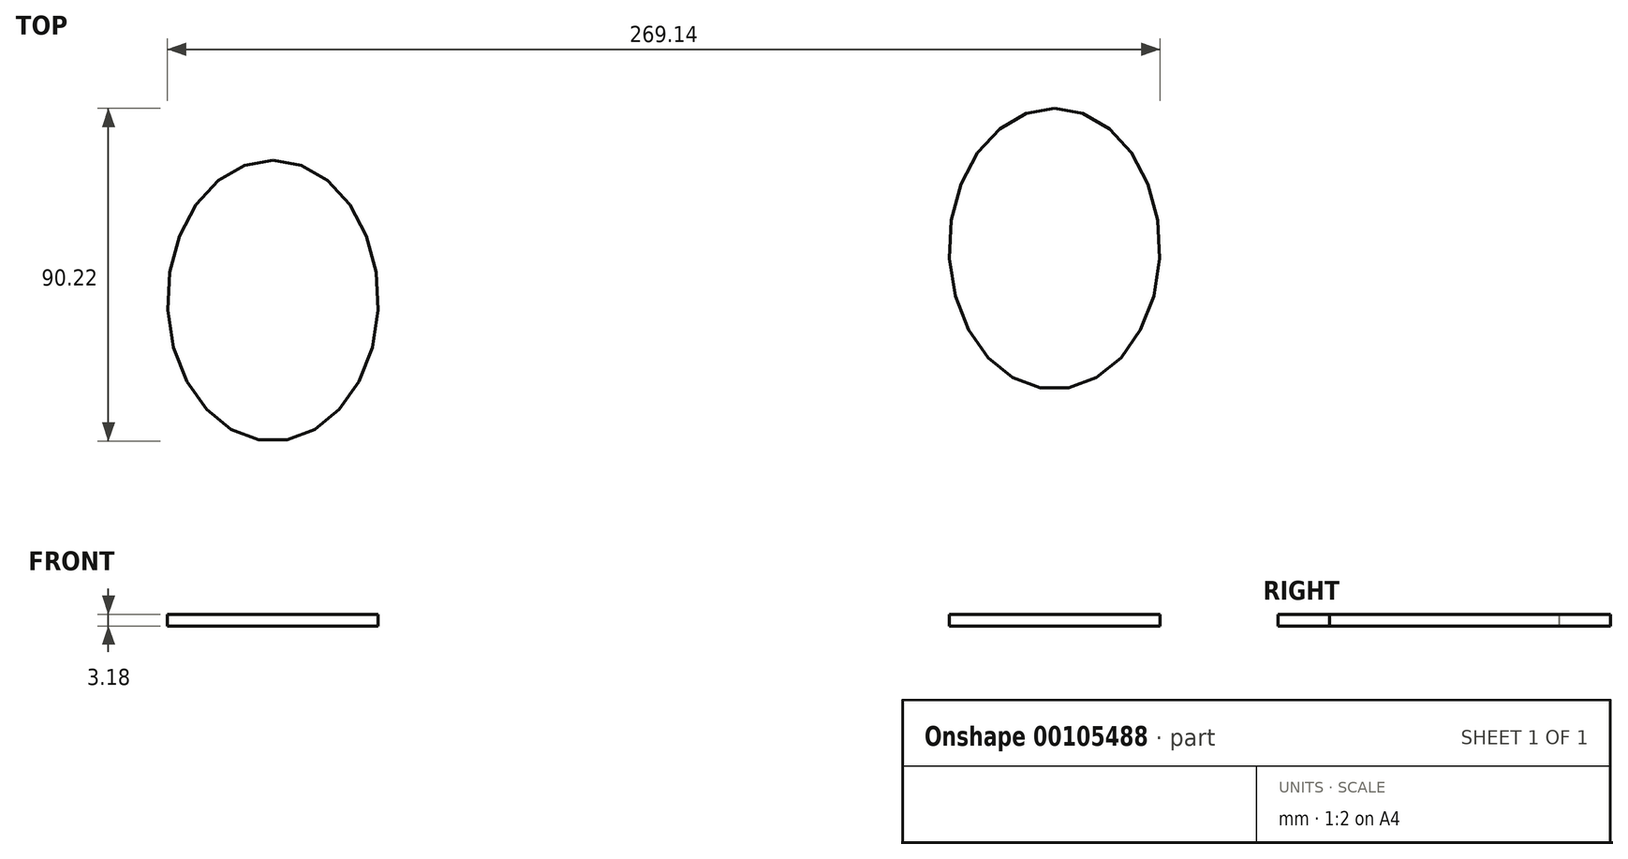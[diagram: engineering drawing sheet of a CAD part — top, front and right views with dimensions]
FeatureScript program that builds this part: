
annotation { "Feature Type Name" : "Feature", "Feature Type Description" : "" }
export const myFeature = defineFeature(function(context is Context, id is Id, definition is map)
    precondition{}
    {
        {
            var Q0;
            Q0=qCreatedBy(makeId("Top.planeOp"),FACE);
            var sketch = newSketch(context, id + "F0", { "sketchPlane" : qUnion([Q0])});
            skEllipse(sketch, "E0", {"center": v(0, 0) * mm, "majorRadius": 38.1 * mm, "minorRadius": 28.58 * mm, "majorAxis": v(0, 1)});
            skFitSpline(sketch, "E1.0", {"points": [v(1.84, 44.4) * mm, v(0, 44.47) * mm, v(-1.84, 44.4) * mm, v(-4.27, 44.17) * mm, v(-7.26, 43.57) * mm, v(-10.72, 42.4) * mm, v(-14.03, 40.82) * mm, v(-17.17, 38.85) * mm, v(-20.1, 36.5) * mm, v(-22.38, 34.26) * mm, v(-24.08, 32.3) * mm, v(-25.3, 30.76) * mm, v(-26.45, 29.15) * mm, v(-27.89, 26.92) * mm, v(-29.5, 24) * mm, v(-31.15, 20.33) * mm, v(-32.51, 16.49) * mm, v(-33.58, 12.51) * mm, v(-34.35, 8.42) * mm, v(-34.74, 4.94) * mm, v(-34.9, 2.13) * mm, v(-34.94, 0) * mm, v(-34.9, -2.13) * mm, v(-34.74, -4.94) * mm, v(-34.35, -8.42) * mm, v(-33.58, -12.51) * mm, v(-32.51, -16.49) * mm, v(-31.15, -20.33) * mm, v(-29.5, -24) * mm, v(-27.89, -26.92) * mm, v(-26.45, -29.15) * mm, v(-25.3, -30.76) * mm, v(-24.08, -32.3) * mm, v(-22.38, -34.26) * mm, v(-20.1, -36.5) * mm, v(-17.17, -38.85) * mm, v(-14.03, -40.82) * mm, v(-10.72, -42.4) * mm, v(-7.26, -43.57) * mm, v(-4.27, -44.17) * mm, v(-1.84, -44.4) * mm, v(0, -44.47) * mm, v(1.84, -44.4) * mm, v(4.27, -44.17) * mm, v(7.26, -43.57) * mm, v(10.72, -42.4) * mm, v(14.03, -40.82) * mm, v(17.17, -38.85) * mm, v(20.1, -36.5) * mm, v(22.38, -34.26) * mm, v(24.08, -32.3) * mm, v(25.3, -30.76) * mm, v(26.45, -29.15) * mm, v(27.89, -26.92) * mm, v(29.5, -24) * mm, v(31.15, -20.33) * mm, v(32.51, -16.49) * mm, v(33.58, -12.51) * mm, v(34.35, -8.42) * mm, v(34.74, -4.94) * mm, v(34.9, -2.13) * mm, v(34.94, 0) * mm, v(34.9, 2.13) * mm, v(34.74, 4.94) * mm, v(34.35, 8.42) * mm, v(33.58, 12.51) * mm, v(32.51, 16.49) * mm, v(31.15, 20.33) * mm, v(29.5, 24) * mm, v(27.89, 26.92) * mm, v(26.45, 29.15) * mm, v(25.3, 30.76) * mm, v(24.08, 32.3) * mm, v(22.38, 34.26) * mm, v(20.1, 36.5) * mm, v(17.17, 38.85) * mm, v(14.03, 40.82) * mm, v(10.72, 42.4) * mm, v(7.26, 43.57) * mm, v(4.27, 44.17) * mm, v(1.84, 44.4) * mm, v(0, 44.47) * mm, v(-1.84, 44.4) * mm, v(1.84, 44.4) * mm]});
            skFitSpline(sketch, "E2.0", {"points": [v(2.26, 50.75) * mm, v(0, 50.82) * mm, v(-2.26, 50.75) * mm, v(-5.24, 50.45) * mm, v(-8.9, 49.72) * mm, v(-13.12, 48.3) * mm, v(-17.12, 46.4) * mm, v(-20.86, 44.03) * mm, v(-24.34, 41.25) * mm, v(-27, 38.63) * mm, v(-28.97, 36.36) * mm, v(-30.38, 34.57) * mm, v(-31.7, 32.72) * mm, v(-33.35, 30.17) * mm, v(-35.19, 26.85) * mm, v(-37.06, 22.69) * mm, v(-38.58, 18.37) * mm, v(-39.78, 13.92) * mm, v(-40.64, 9.37) * mm, v(-41.07, 5.5) * mm, v(-41.25, 2.36) * mm, v(-41.29, 0) * mm, v(-41.25, -2.36) * mm, v(-41.07, -5.5) * mm, v(-40.64, -9.37) * mm, v(-39.78, -13.92) * mm, v(-38.58, -18.37) * mm, v(-37.06, -22.69) * mm, v(-35.19, -26.85) * mm, v(-33.35, -30.17) * mm, v(-31.7, -32.72) * mm, v(-30.38, -34.57) * mm, v(-28.97, -36.36) * mm, v(-27, -38.63) * mm, v(-24.34, -41.25) * mm, v(-20.86, -44.03) * mm, v(-17.12, -46.4) * mm, v(-13.12, -48.3) * mm, v(-8.9, -49.72) * mm, v(-5.24, -50.45) * mm, v(-2.26, -50.75) * mm, v(0, -50.82) * mm, v(2.26, -50.75) * mm, v(5.24, -50.45) * mm, v(8.9, -49.72) * mm, v(13.12, -48.3) * mm, v(17.12, -46.4) * mm, v(20.86, -44.03) * mm, v(24.34, -41.25) * mm, v(27, -38.63) * mm, v(28.97, -36.36) * mm, v(30.38, -34.57) * mm, v(31.7, -32.72) * mm, v(33.35, -30.17) * mm, v(35.19, -26.85) * mm, v(37.06, -22.69) * mm, v(38.58, -18.37) * mm, v(39.78, -13.92) * mm, v(40.64, -9.37) * mm, v(41.07, -5.5) * mm, v(41.25, -2.36) * mm, v(41.29, 0) * mm, v(41.25, 2.36) * mm, v(41.07, 5.5) * mm, v(40.64, 9.37) * mm, v(39.78, 13.92) * mm, v(38.58, 18.37) * mm, v(37.06, 22.69) * mm, v(35.19, 26.85) * mm, v(33.35, 30.17) * mm, v(31.7, 32.72) * mm, v(30.38, 34.57) * mm, v(28.97, 36.36) * mm, v(27, 38.63) * mm, v(24.34, 41.25) * mm, v(20.86, 44.03) * mm, v(17.12, 46.4) * mm, v(13.12, 48.3) * mm, v(8.9, 49.72) * mm, v(5.24, 50.45) * mm, v(2.26, 50.75) * mm, v(0, 50.82) * mm, v(-2.26, 50.75) * mm, v(2.26, 50.75) * mm]});
            skFitSpline(sketch, "E3.0", {"points": [v(2.68, 57.1) * mm, v(0, 57.18) * mm, v(-2.68, 57.1) * mm, v(-6.22, 56.74) * mm, v(-10.54, 55.87) * mm, v(-15.51, 54.2) * mm, v(-20.2, 51.96) * mm, v(-24.56, 49.2) * mm, v(-28.57, 46) * mm, v(-31.61, 43) * mm, v(-33.86, 40.4) * mm, v(-35.46, 38.38) * mm, v(-36.96, 36.28) * mm, v(-38.82, 33.41) * mm, v(-40.88, 29.69) * mm, v(-42.96, 25.05) * mm, v(-44.65, 20.25) * mm, v(-45.98, 15.33) * mm, v(-46.92, 10.3) * mm, v(-47.4, 6.04) * mm, v(-47.6, 2.6) * mm, v(-47.64, 0) * mm, v(-47.6, -2.6) * mm, v(-47.4, -6.04) * mm, v(-46.92, -10.3) * mm, v(-45.98, -15.33) * mm, v(-44.65, -20.25) * mm, v(-42.96, -25.05) * mm, v(-40.88, -29.69) * mm, v(-38.82, -33.41) * mm, v(-36.96, -36.28) * mm, v(-35.46, -38.38) * mm, v(-33.86, -40.4) * mm, v(-31.61, -43) * mm, v(-28.57, -46) * mm, v(-24.56, -49.2) * mm, v(-20.2, -51.96) * mm, v(-15.51, -54.2) * mm, v(-10.54, -55.87) * mm, v(-6.22, -56.74) * mm, v(-2.68, -57.1) * mm, v(0, -57.18) * mm, v(2.68, -57.1) * mm, v(6.22, -56.74) * mm, v(10.54, -55.87) * mm, v(15.51, -54.2) * mm, v(20.2, -51.96) * mm, v(24.56, -49.2) * mm, v(28.57, -46) * mm, v(31.61, -43) * mm, v(33.86, -40.4) * mm, v(35.46, -38.38) * mm, v(36.96, -36.28) * mm, v(38.82, -33.41) * mm, v(40.88, -29.69) * mm, v(42.96, -25.05) * mm, v(44.65, -20.25) * mm, v(45.98, -15.33) * mm, v(46.92, -10.3) * mm, v(47.4, -6.04) * mm, v(47.6, -2.6) * mm, v(47.64, 0) * mm, v(47.6, 2.6) * mm, v(47.4, 6.04) * mm, v(46.92, 10.3) * mm, v(45.98, 15.33) * mm, v(44.65, 20.25) * mm, v(42.96, 25.05) * mm, v(40.88, 29.69) * mm, v(38.82, 33.41) * mm, v(36.96, 36.28) * mm, v(35.46, 38.38) * mm, v(33.86, 40.4) * mm, v(31.61, 43) * mm, v(28.57, 46) * mm, v(24.56, 49.2) * mm, v(20.2, 51.96) * mm, v(15.51, 54.2) * mm, v(10.54, 55.87) * mm, v(6.22, 56.74) * mm, v(2.68, 57.1) * mm, v(0, 57.18) * mm, v(-2.68, 57.1) * mm, v(2.68, 57.1) * mm]});
            skFitSpline(sketch, "E4.0", {"points": [v(3.1, 63.43) * mm, v(0, 63.53) * mm, v(-3.1, 63.43) * mm, v(-7.19, 63.02) * mm, v(-12.19, 62.03) * mm, v(-17.91, 60.1) * mm, v(-23.28, 57.53) * mm, v(-28.25, 54.39) * mm, v(-32.8, 50.75) * mm, v(-36.23, 47.36) * mm, v(-38.76, 44.46) * mm, v(-40.54, 42.2) * mm, v(-42.22, 39.85) * mm, v(-44.28, 36.65) * mm, v(-46.57, 32.53) * mm, v(-48.86, 27.4) * mm, v(-50.73, 22.14) * mm, v(-52.17, 16.74) * mm, v(-53.2, 11.25) * mm, v(-53.73, 6.6) * mm, v(-53.94, 2.84) * mm, v(-54, 0) * mm, v(-53.94, -2.84) * mm, v(-53.73, -6.6) * mm, v(-53.2, -11.25) * mm, v(-52.17, -16.74) * mm, v(-50.73, -22.14) * mm, v(-48.86, -27.4) * mm, v(-46.57, -32.53) * mm, v(-44.28, -36.65) * mm, v(-42.22, -39.85) * mm, v(-40.54, -42.2) * mm, v(-38.76, -44.46) * mm, v(-36.23, -47.36) * mm, v(-32.8, -50.75) * mm, v(-28.25, -54.39) * mm, v(-23.28, -57.53) * mm, v(-17.91, -60.1) * mm, v(-12.19, -62.03) * mm, v(-7.19, -63.02) * mm, v(-3.1, -63.43) * mm, v(0, -63.53) * mm, v(3.1, -63.43) * mm, v(7.19, -63.02) * mm, v(12.19, -62.03) * mm, v(17.91, -60.1) * mm, v(23.28, -57.53) * mm, v(28.25, -54.39) * mm, v(32.8, -50.75) * mm, v(36.23, -47.36) * mm, v(38.76, -44.46) * mm, v(40.54, -42.2) * mm, v(42.22, -39.85) * mm, v(44.28, -36.65) * mm, v(46.57, -32.53) * mm, v(48.86, -27.4) * mm, v(50.73, -22.14) * mm, v(52.17, -16.74) * mm, v(53.2, -11.25) * mm, v(53.73, -6.6) * mm, v(53.94, -2.84) * mm, v(54, 0) * mm, v(53.94, 2.84) * mm, v(53.73, 6.6) * mm, v(53.2, 11.25) * mm, v(52.17, 16.74) * mm, v(50.73, 22.14) * mm, v(48.86, 27.4) * mm, v(46.57, 32.53) * mm, v(44.28, 36.65) * mm, v(42.22, 39.85) * mm, v(40.54, 42.2) * mm, v(38.76, 44.46) * mm, v(36.23, 47.36) * mm, v(32.8, 50.75) * mm, v(28.25, 54.39) * mm, v(23.28, 57.53) * mm, v(17.91, 60.1) * mm, v(12.19, 62.03) * mm, v(7.19, 63.02) * mm, v(3.1, 63.43) * mm, v(0, 63.53) * mm, v(-3.1, 63.43) * mm, v(3.1, 63.43) * mm]});
            skFitSpline(sketch, "E5.0", {"points": [v(3.52, 69.77) * mm, v(0, 69.89) * mm, v(-3.52, 69.77) * mm, v(-8.16, 69.31) * mm, v(-13.83, 68.18) * mm, v(-20.3, 66) * mm, v(-26.36, 63.1) * mm, v(-31.95, 59.57) * mm, v(-37.03, 55.5) * mm, v(-40.85, 51.73) * mm, v(-43.65, 48.51) * mm, v(-45.63, 46) * mm, v(-47.47, 43.42) * mm, v(-49.75, 39.9) * mm, v(-52.25, 35.37) * mm, v(-54.76, 29.76) * mm, v(-56.8, 24.02) * mm, v(-58.37, 18.16) * mm, v(-59.5, 12.19) * mm, v(-60.06, 7.14) * mm, v(-60.29, 3.07) * mm, v(-60.34, 0) * mm, v(-60.29, -3.07) * mm, v(-60.06, -7.14) * mm, v(-59.5, -12.19) * mm, v(-58.37, -18.16) * mm, v(-56.8, -24.02) * mm, v(-54.76, -29.76) * mm, v(-52.25, -35.37) * mm, v(-49.75, -39.9) * mm, v(-47.47, -43.42) * mm, v(-45.63, -46) * mm, v(-43.65, -48.51) * mm, v(-40.85, -51.73) * mm, v(-37.03, -55.5) * mm, v(-31.95, -59.57) * mm, v(-26.36, -63.1) * mm, v(-20.3, -66) * mm, v(-13.83, -68.18) * mm, v(-8.16, -69.31) * mm, v(-3.52, -69.77) * mm, v(0, -69.89) * mm, v(3.52, -69.77) * mm, v(8.16, -69.31) * mm, v(13.83, -68.18) * mm, v(20.3, -66) * mm, v(26.36, -63.1) * mm, v(31.95, -59.57) * mm, v(37.03, -55.5) * mm, v(40.85, -51.73) * mm, v(43.65, -48.51) * mm, v(45.63, -46) * mm, v(47.47, -43.42) * mm, v(49.75, -39.9) * mm, v(52.25, -35.37) * mm, v(54.76, -29.76) * mm, v(56.8, -24.02) * mm, v(58.37, -18.16) * mm, v(59.5, -12.19) * mm, v(60.06, -7.14) * mm, v(60.29, -3.07) * mm, v(60.34, 0) * mm, v(60.29, 3.07) * mm, v(60.06, 7.14) * mm, v(59.5, 12.19) * mm, v(58.37, 18.16) * mm, v(56.8, 24.02) * mm, v(54.76, 29.76) * mm, v(52.25, 35.37) * mm, v(49.75, 39.9) * mm, v(47.47, 43.42) * mm, v(45.63, 46) * mm, v(43.65, 48.51) * mm, v(40.85, 51.73) * mm, v(37.03, 55.5) * mm, v(31.95, 59.57) * mm, v(26.36, 63.1) * mm, v(20.3, 66) * mm, v(13.83, 68.18) * mm, v(8.16, 69.31) * mm, v(3.52, 69.77) * mm, v(0, 69.89) * mm, v(-3.52, 69.77) * mm, v(3.52, 69.77) * mm]});
            skFitSpline(sketch, "E6.0", {"points": [v(3.94, 76.11) * mm, v(0, 76.24) * mm, v(-3.94, 76.11) * mm, v(-9.14, 75.6) * mm, v(-15.48, 74.33) * mm, v(-22.7, 71.9) * mm, v(-29.45, 68.67) * mm, v(-35.64, 64.75) * mm, v(-41.27, 60.25) * mm, v(-45.47, 56.1) * mm, v(-48.54, 52.56) * mm, v(-50.71, 49.81) * mm, v(-52.73, 46.99) * mm, v(-55.21, 43.14) * mm, v(-57.94, 38.2) * mm, v(-60.67, 32.12) * mm, v(-62.87, 25.9) * mm, v(-64.57, 19.57) * mm, v(-65.78, 13.13) * mm, v(-66.39, 7.7) * mm, v(-66.63, 3.3) * mm, v(-66.7, 0) * mm, v(-66.63, -3.3) * mm, v(-66.39, -7.7) * mm, v(-65.78, -13.13) * mm, v(-64.57, -19.57) * mm, v(-62.87, -25.9) * mm, v(-60.67, -32.12) * mm, v(-57.94, -38.2) * mm, v(-55.21, -43.14) * mm, v(-52.73, -46.99) * mm, v(-50.71, -49.81) * mm, v(-48.54, -52.56) * mm, v(-45.47, -56.1) * mm, v(-41.27, -60.25) * mm, v(-35.64, -64.75) * mm, v(-29.45, -68.67) * mm, v(-22.7, -71.9) * mm, v(-15.48, -74.33) * mm, v(-9.14, -75.6) * mm, v(-3.94, -76.11) * mm, v(0, -76.24) * mm, v(3.94, -76.11) * mm, v(9.14, -75.6) * mm, v(15.48, -74.33) * mm, v(22.7, -71.9) * mm, v(29.45, -68.67) * mm, v(35.64, -64.75) * mm, v(41.27, -60.25) * mm, v(45.47, -56.1) * mm, v(48.54, -52.56) * mm, v(50.71, -49.81) * mm, v(52.73, -46.99) * mm, v(55.21, -43.14) * mm, v(57.94, -38.2) * mm, v(60.67, -32.12) * mm, v(62.87, -25.9) * mm, v(64.57, -19.57) * mm, v(65.78, -13.13) * mm, v(66.39, -7.7) * mm, v(66.63, -3.3) * mm, v(66.7, 0) * mm, v(66.63, 3.3) * mm, v(66.39, 7.7) * mm, v(65.78, 13.13) * mm, v(64.57, 19.57) * mm, v(62.87, 25.9) * mm, v(60.67, 32.12) * mm, v(57.94, 38.2) * mm, v(55.21, 43.14) * mm, v(52.73, 46.99) * mm, v(50.71, 49.81) * mm, v(48.54, 52.56) * mm, v(45.47, 56.1) * mm, v(41.27, 60.25) * mm, v(35.64, 64.75) * mm, v(29.45, 68.67) * mm, v(22.7, 71.9) * mm, v(15.48, 74.33) * mm, v(9.14, 75.6) * mm, v(3.94, 76.11) * mm, v(0, 76.24) * mm, v(-3.94, 76.11) * mm, v(3.94, 76.11) * mm]});
            skFitSpline(sketch, "E7.0", {"points": [v(4.36, 82.45) * mm, v(0, 82.6) * mm, v(-4.36, 82.45) * mm, v(-10.1, 81.88) * mm, v(-17.12, 80.48) * mm, v(-25.1, 77.8) * mm, v(-32.53, 74.23) * mm, v(-39.34, 69.93) * mm, v(-45.5, 65) * mm, v(-50.09, 60.47) * mm, v(-53.44, 56.61) * mm, v(-55.8, 53.62) * mm, v(-57.98, 50.55) * mm, v(-60.67, 46.38) * mm, v(-63.63, 41.05) * mm, v(-66.57, 34.48) * mm, v(-68.94, 27.79) * mm, v(-70.77, 20.98) * mm, v(-72.07, 14.07) * mm, v(-72.72, 8.25) * mm, v(-72.98, 3.54) * mm, v(-73.05, 0) * mm, v(-72.98, -3.54) * mm, v(-72.72, -8.25) * mm, v(-72.07, -14.07) * mm, v(-70.77, -20.98) * mm, v(-68.94, -27.79) * mm, v(-66.57, -34.48) * mm, v(-63.63, -41.05) * mm, v(-60.67, -46.38) * mm, v(-57.98, -50.55) * mm, v(-55.8, -53.62) * mm, v(-53.44, -56.61) * mm, v(-50.09, -60.47) * mm, v(-45.5, -65) * mm, v(-39.34, -69.93) * mm, v(-32.53, -74.23) * mm, v(-25.1, -77.8) * mm, v(-17.12, -80.48) * mm, v(-10.1, -81.88) * mm, v(-4.36, -82.45) * mm, v(0, -82.6) * mm, v(4.36, -82.45) * mm, v(10.1, -81.88) * mm, v(17.12, -80.48) * mm, v(25.1, -77.8) * mm, v(32.53, -74.23) * mm, v(39.34, -69.93) * mm, v(45.5, -65) * mm, v(50.09, -60.47) * mm, v(53.44, -56.61) * mm, v(55.8, -53.62) * mm, v(57.98, -50.55) * mm, v(60.67, -46.38) * mm, v(63.63, -41.05) * mm, v(66.57, -34.48) * mm, v(68.94, -27.79) * mm, v(70.77, -20.98) * mm, v(72.07, -14.07) * mm, v(72.72, -8.25) * mm, v(72.98, -3.54) * mm, v(73.05, 0) * mm, v(72.98, 3.54) * mm, v(72.72, 8.25) * mm, v(72.07, 14.07) * mm, v(70.77, 20.98) * mm, v(68.94, 27.79) * mm, v(66.57, 34.48) * mm, v(63.63, 41.05) * mm, v(60.67, 46.38) * mm, v(57.98, 50.55) * mm, v(55.8, 53.62) * mm, v(53.44, 56.61) * mm, v(50.09, 60.47) * mm, v(45.5, 65) * mm, v(39.34, 69.93) * mm, v(32.53, 74.23) * mm, v(25.1, 77.8) * mm, v(17.12, 80.48) * mm, v(10.1, 81.88) * mm, v(4.36, 82.45) * mm, v(0, 82.6) * mm, v(-4.36, 82.45) * mm, v(4.36, 82.45) * mm]});
            skFitSpline(sketch, "E8.0", {"points": [v(4.78, 88.8) * mm, v(0, 88.95) * mm, v(-4.78, 88.8) * mm, v(-11.08, 88.17) * mm, v(-18.76, 86.63) * mm, v(-27.5, 83.7) * mm, v(-35.6, 79.8) * mm, v(-43.03, 75.11) * mm, v(-49.73, 69.76) * mm, v(-54.7, 64.83) * mm, v(-58.33, 60.67) * mm, v(-60.88, 57.43) * mm, v(-63.24, 54.12) * mm, v(-66.14, 49.63) * mm, v(-69.32, 43.89) * mm, v(-72.47, 36.84) * mm, v(-75.01, 29.67) * mm, v(-76.96, 22.39) * mm, v(-78.35, 15.01) * mm, v(-79.05, 8.8) * mm, v(-79.33, 3.78) * mm, v(-79.4, 0) * mm, v(-79.33, -3.78) * mm, v(-79.05, -8.8) * mm, v(-78.35, -15.01) * mm, v(-76.96, -22.39) * mm, v(-75.01, -29.67) * mm, v(-72.47, -36.84) * mm, v(-69.32, -43.89) * mm, v(-66.14, -49.63) * mm, v(-63.24, -54.12) * mm, v(-60.88, -57.43) * mm, v(-58.33, -60.67) * mm, v(-54.7, -64.83) * mm, v(-49.73, -69.76) * mm, v(-43.03, -75.11) * mm, v(-35.6, -79.8) * mm, v(-27.5, -83.7) * mm, v(-18.76, -86.63) * mm, v(-11.08, -88.17) * mm, v(-4.78, -88.8) * mm, v(0, -88.95) * mm, v(4.78, -88.8) * mm, v(11.08, -88.17) * mm, v(18.76, -86.63) * mm, v(27.5, -83.7) * mm, v(35.6, -79.8) * mm, v(43.03, -75.11) * mm, v(49.73, -69.76) * mm, v(54.7, -64.83) * mm, v(58.33, -60.67) * mm, v(60.88, -57.43) * mm, v(63.24, -54.12) * mm, v(66.14, -49.63) * mm, v(69.32, -43.89) * mm, v(72.47, -36.84) * mm, v(75.01, -29.67) * mm, v(76.96, -22.39) * mm, v(78.35, -15.01) * mm, v(79.05, -8.8) * mm, v(79.33, -3.78) * mm, v(79.4, 0) * mm, v(79.33, 3.78) * mm, v(79.05, 8.8) * mm, v(78.35, 15.01) * mm, v(76.96, 22.39) * mm, v(75.01, 29.67) * mm, v(72.47, 36.84) * mm, v(69.32, 43.89) * mm, v(66.14, 49.63) * mm, v(63.24, 54.12) * mm, v(60.88, 57.43) * mm, v(58.33, 60.67) * mm, v(54.7, 64.83) * mm, v(49.73, 69.76) * mm, v(43.03, 75.11) * mm, v(35.6, 79.8) * mm, v(27.5, 83.7) * mm, v(18.76, 86.63) * mm, v(11.08, 88.17) * mm, v(4.78, 88.8) * mm, v(0, 88.95) * mm, v(-4.78, 88.8) * mm, v(4.78, 88.8) * mm]});
            skFitSpline(sketch, "E9.0", {"points": [v(5.2, 95.14) * mm, v(0, 95.3) * mm, v(-5.2, 95.14) * mm, v(-12.06, 94.45) * mm, v(-20.4, 92.78) * mm, v(-29.9, 89.59) * mm, v(-38.7, 85.37) * mm, v(-46.72, 80.3) * mm, v(-53.96, 74.5) * mm, v(-59.32, 69.2) * mm, v(-63.22, 64.72) * mm, v(-65.96, 61.24) * mm, v(-68.5, 57.69) * mm, v(-71.6, 52.87) * mm, v(-75, 46.73) * mm, v(-78.38, 39.2) * mm, v(-81.08, 31.55) * mm, v(-83.16, 23.8) * mm, v(-84.64, 15.96) * mm, v(-85.38, 9.35) * mm, v(-85.68, 4.02) * mm, v(-85.75, 0) * mm, v(-85.68, -4.02) * mm, v(-85.38, -9.35) * mm, v(-84.64, -15.96) * mm, v(-83.16, -23.8) * mm, v(-81.08, -31.55) * mm, v(-78.38, -39.2) * mm, v(-75, -46.73) * mm, v(-71.6, -52.87) * mm, v(-68.5, -57.69) * mm, v(-65.96, -61.24) * mm, v(-63.22, -64.72) * mm, v(-59.32, -69.2) * mm, v(-53.96, -74.5) * mm, v(-46.72, -80.3) * mm, v(-38.7, -85.37) * mm, v(-29.9, -89.59) * mm, v(-20.4, -92.78) * mm, v(-12.06, -94.45) * mm, v(-5.2, -95.14) * mm, v(0, -95.3) * mm, v(5.2, -95.14) * mm, v(12.06, -94.45) * mm, v(20.4, -92.78) * mm, v(29.9, -89.59) * mm, v(38.7, -85.37) * mm, v(46.72, -80.3) * mm, v(53.96, -74.5) * mm, v(59.32, -69.2) * mm, v(63.22, -64.72) * mm, v(65.96, -61.24) * mm, v(68.5, -57.69) * mm, v(71.6, -52.87) * mm, v(75, -46.73) * mm, v(78.38, -39.2) * mm, v(81.08, -31.55) * mm, v(83.16, -23.8) * mm, v(84.64, -15.96) * mm, v(85.38, -9.35) * mm, v(85.68, -4.02) * mm, v(85.75, 0) * mm, v(85.68, 4.02) * mm, v(85.38, 9.35) * mm, v(84.64, 15.96) * mm, v(83.16, 23.8) * mm, v(81.08, 31.55) * mm, v(78.38, 39.2) * mm, v(75, 46.73) * mm, v(71.6, 52.87) * mm, v(68.5, 57.69) * mm, v(65.96, 61.24) * mm, v(63.22, 64.72) * mm, v(59.32, 69.2) * mm, v(53.96, 74.5) * mm, v(46.72, 80.3) * mm, v(38.7, 85.37) * mm, v(29.9, 89.59) * mm, v(20.4, 92.78) * mm, v(12.06, 94.45) * mm, v(5.2, 95.14) * mm, v(0, 95.3) * mm, v(-5.2, 95.14) * mm, v(5.2, 95.14) * mm]});
            skFitSpline(sketch, "E10.0", {"points": [v(5.62, 101.48) * mm, v(0, 101.66) * mm, v(-5.62, 101.48) * mm, v(-13.03, 100.74) * mm, v(-22.05, 98.93) * mm, v(-32.29, 95.49) * mm, v(-41.77, 90.94) * mm, v(-50.42, 85.47) * mm, v(-58.2, 79.26) * mm, v(-63.94, 73.57) * mm, v(-68.12, 68.77) * mm, v(-71.04, 65.06) * mm, v(-73.75, 61.26) * mm, v(-77.07, 56.12) * mm, v(-80.7, 49.57) * mm, v(-84.28, 41.56) * mm, v(-87.15, 33.44) * mm, v(-89.36, 25.21) * mm, v(-90.92, 16.9) * mm, v(-91.7, 9.9) * mm, v(-92.02, 4.25) * mm, v(-92.1, 0) * mm, v(-92.02, -4.25) * mm, v(-91.7, -9.9) * mm, v(-90.92, -16.9) * mm, v(-89.36, -25.21) * mm, v(-87.15, -33.44) * mm, v(-84.28, -41.56) * mm, v(-80.7, -49.57) * mm, v(-77.07, -56.12) * mm, v(-73.75, -61.26) * mm, v(-71.04, -65.06) * mm, v(-68.12, -68.77) * mm, v(-63.94, -73.57) * mm, v(-58.2, -79.26) * mm, v(-50.42, -85.47) * mm, v(-41.77, -90.94) * mm, v(-32.29, -95.49) * mm, v(-22.05, -98.93) * mm, v(-13.03, -100.74) * mm, v(-5.62, -101.48) * mm, v(0, -101.66) * mm, v(5.62, -101.48) * mm, v(13.03, -100.74) * mm, v(22.05, -98.93) * mm, v(32.29, -95.49) * mm, v(41.77, -90.94) * mm, v(50.42, -85.47) * mm, v(58.2, -79.26) * mm, v(63.94, -73.57) * mm, v(68.12, -68.77) * mm, v(71.04, -65.06) * mm, v(73.75, -61.26) * mm, v(77.07, -56.12) * mm, v(80.7, -49.57) * mm, v(84.28, -41.56) * mm, v(87.15, -33.44) * mm, v(89.36, -25.21) * mm, v(90.92, -16.9) * mm, v(91.7, -9.9) * mm, v(92.02, -4.25) * mm, v(92.1, 0) * mm, v(92.02, 4.25) * mm, v(91.7, 9.9) * mm, v(90.92, 16.9) * mm, v(89.36, 25.21) * mm, v(87.15, 33.44) * mm, v(84.28, 41.56) * mm, v(80.7, 49.57) * mm, v(77.07, 56.12) * mm, v(73.75, 61.26) * mm, v(71.04, 65.06) * mm, v(68.12, 68.77) * mm, v(63.94, 73.57) * mm, v(58.2, 79.26) * mm, v(50.42, 85.47) * mm, v(41.77, 90.94) * mm, v(32.29, 95.49) * mm, v(22.05, 98.93) * mm, v(13.03, 100.74) * mm, v(5.62, 101.48) * mm, v(0, 101.66) * mm, v(-5.62, 101.48) * mm, v(5.62, 101.48) * mm]});
            skEllipse(sketch, "E11", {"center": v(211.98, 14.02) * mm, "majorRadius": 38.1 * mm, "minorRadius": 28.58 * mm, "majorAxis": v(0, 1)});
            skFitSpline(sketch, "E12.0", {"points": [v(213.61, 55.25) * mm, v(211.98, 55.3) * mm, v(210.36, 55.25) * mm, v(208.2, 55.04) * mm, v(205.55, 54.51) * mm, v(202.46, 53.47) * mm, v(199.5, 52.05) * mm, v(196.66, 50.27) * mm, v(194, 48.14) * mm, v(191.92, 46.1) * mm, v(190.35, 44.3) * mm, v(189.23, 42.87) * mm, v(188.16, 41.38) * mm, v(186.83, 39.32) * mm, v(185.33, 36.6) * mm, v(183.78, 33.16) * mm, v(182.5, 29.56) * mm, v(181.5, 25.82) * mm, v(180.78, 21.97) * mm, v(180.4, 18.68) * mm, v(180.26, 16.02) * mm, v(180.22, 14.02) * mm, v(180.26, 12) * mm, v(180.4, 9.35) * mm, v(180.78, 6.06) * mm, v(181.5, 2.2) * mm, v(182.5, -1.53) * mm, v(183.78, -5.13) * mm, v(185.33, -8.57) * mm, v(186.83, -11.29) * mm, v(188.16, -13.35) * mm, v(189.23, -14.84) * mm, v(190.35, -16.27) * mm, v(191.92, -18.06) * mm, v(194, -20.11) * mm, v(196.66, -22.24) * mm, v(199.5, -24.02) * mm, v(202.46, -25.44) * mm, v(205.55, -26.48) * mm, v(208.2, -27.01) * mm, v(210.36, -27.22) * mm, v(211.98, -27.28) * mm, v(213.61, -27.22) * mm, v(215.77, -27.01) * mm, v(218.42, -26.48) * mm, v(221.5, -25.44) * mm, v(224.48, -24.02) * mm, v(227.3, -22.24) * mm, v(229.98, -20.11) * mm, v(232.05, -18.06) * mm, v(233.62, -16.27) * mm, v(234.74, -14.84) * mm, v(235.8, -13.35) * mm, v(237.14, -11.29) * mm, v(238.64, -8.57) * mm, v(240.18, -5.13) * mm, v(241.46, -1.53) * mm, v(242.47, 2.2) * mm, v(243.2, 6.06) * mm, v(243.56, 9.35) * mm, v(243.7, 12) * mm, v(243.75, 14.02) * mm, v(243.7, 16.02) * mm, v(243.56, 18.68) * mm, v(243.2, 21.97) * mm, v(242.47, 25.82) * mm, v(241.46, 29.56) * mm, v(240.18, 33.16) * mm, v(238.64, 36.6) * mm, v(237.14, 39.32) * mm, v(235.8, 41.38) * mm, v(234.74, 42.87) * mm, v(233.62, 44.3) * mm, v(232.05, 46.1) * mm, v(229.98, 48.14) * mm, v(227.3, 50.27) * mm, v(224.48, 52.05) * mm, v(221.5, 53.47) * mm, v(218.42, 54.51) * mm, v(215.77, 55.04) * mm, v(213.61, 55.25) * mm, v(211.98, 55.3) * mm, v(210.36, 55.25) * mm, v(213.61, 55.25) * mm]});
            skFitSpline(sketch, "E13.0", {"points": [v(214.03, 61.6) * mm, v(211.98, 61.66) * mm, v(209.94, 61.6) * mm, v(207.23, 61.33) * mm, v(203.9, 60.66) * mm, v(200.06, 59.37) * mm, v(196.4, 57.62) * mm, v(192.97, 55.45) * mm, v(189.76, 52.9) * mm, v(187.3, 50.46) * mm, v(185.46, 48.35) * mm, v(184.15, 46.68) * mm, v(182.9, 44.95) * mm, v(181.37, 42.56) * mm, v(179.64, 39.44) * mm, v(177.88, 35.52) * mm, v(176.44, 31.44) * mm, v(175.3, 27.23) * mm, v(174.5, 22.9) * mm, v(174.08, 19.23) * mm, v(173.91, 16.26) * mm, v(173.87, 14.02) * mm, v(173.91, 11.77) * mm, v(174.08, 8.8) * mm, v(174.5, 5.12) * mm, v(175.3, 0.8) * mm, v(176.44, -3.41) * mm, v(177.88, -7.5) * mm, v(179.64, -11.41) * mm, v(181.37, -14.53) * mm, v(182.9, -16.92) * mm, v(184.15, -18.65) * mm, v(185.46, -20.32) * mm, v(187.3, -22.43) * mm, v(189.76, -24.86) * mm, v(192.97, -27.42) * mm, v(196.4, -29.6) * mm, v(200.06, -31.34) * mm, v(203.9, -32.63) * mm, v(207.23, -33.3) * mm, v(209.94, -33.56) * mm, v(211.98, -33.63) * mm, v(214.03, -33.56) * mm, v(216.74, -33.3) * mm, v(220.06, -32.63) * mm, v(223.9, -31.34) * mm, v(227.56, -29.6) * mm, v(231, -27.42) * mm, v(234.2, -24.86) * mm, v(236.67, -22.43) * mm, v(238.5, -20.32) * mm, v(239.82, -18.65) * mm, v(241.06, -16.92) * mm, v(242.6, -14.53) * mm, v(244.33, -11.41) * mm, v(246.09, -7.5) * mm, v(247.53, -3.41) * mm, v(248.66, 0.8) * mm, v(249.48, 5.12) * mm, v(249.89, 8.8) * mm, v(250.06, 11.77) * mm, v(250.1, 14.02) * mm, v(250.06, 16.26) * mm, v(249.89, 19.23) * mm, v(249.48, 22.9) * mm, v(248.66, 27.23) * mm, v(247.53, 31.44) * mm, v(246.09, 35.52) * mm, v(244.33, 39.44) * mm, v(242.6, 42.56) * mm, v(241.06, 44.95) * mm, v(239.82, 46.68) * mm, v(238.5, 48.35) * mm, v(236.67, 50.46) * mm, v(234.2, 52.9) * mm, v(231, 55.45) * mm, v(227.56, 57.62) * mm, v(223.9, 59.37) * mm, v(220.06, 60.66) * mm, v(216.74, 61.33) * mm, v(214.03, 61.6) * mm, v(211.98, 61.66) * mm, v(209.94, 61.6) * mm, v(214.03, 61.6) * mm]});
            skFitSpline(sketch, "E14.0", {"points": [v(214.45, 67.94) * mm, v(211.98, 68.02) * mm, v(209.52, 67.94) * mm, v(206.26, 67.61) * mm, v(202.26, 66.81) * mm, v(197.67, 65.27) * mm, v(193.33, 63.2) * mm, v(189.27, 60.63) * mm, v(185.53, 57.64) * mm, v(182.68, 54.83) * mm, v(180.57, 52.4) * mm, v(179.06, 50.5) * mm, v(177.65, 48.51) * mm, v(175.9, 45.8) * mm, v(173.95, 42.28) * mm, v(171.98, 37.88) * mm, v(170.36, 33.33) * mm, v(169.1, 28.64) * mm, v(168.2, 23.85) * mm, v(167.75, 19.78) * mm, v(167.56, 16.5) * mm, v(167.52, 14.02) * mm, v(167.56, 11.53) * mm, v(167.75, 8.25) * mm, v(168.2, 4.18) * mm, v(169.1, -0.61) * mm, v(170.36, -5.3) * mm, v(171.98, -9.85) * mm, v(173.95, -14.25) * mm, v(175.9, -17.77) * mm, v(177.65, -20.48) * mm, v(179.06, -22.46) * mm, v(180.57, -24.37) * mm, v(182.68, -26.8) * mm, v(185.53, -29.61) * mm, v(189.27, -32.6) * mm, v(193.33, -35.16) * mm, v(197.67, -37.24) * mm, v(202.26, -38.78) * mm, v(206.26, -39.58) * mm, v(209.52, -39.9) * mm, v(211.98, -39.99) * mm, v(214.45, -39.9) * mm, v(217.71, -39.58) * mm, v(221.7, -38.78) * mm, v(226.3, -37.24) * mm, v(230.64, -35.16) * mm, v(234.7, -32.6) * mm, v(238.44, -29.61) * mm, v(241.29, -26.8) * mm, v(243.4, -24.37) * mm, v(244.9, -22.46) * mm, v(246.32, -20.48) * mm, v(248.07, -17.77) * mm, v(250.02, -14.25) * mm, v(252, -9.85) * mm, v(253.6, -5.3) * mm, v(254.86, -0.61) * mm, v(255.76, 4.18) * mm, v(256.22, 8.25) * mm, v(256.4, 11.53) * mm, v(256.45, 14.02) * mm, v(256.4, 16.5) * mm, v(256.22, 19.78) * mm, v(255.76, 23.85) * mm, v(254.86, 28.64) * mm, v(253.6, 33.33) * mm, v(252, 37.88) * mm, v(250.02, 42.28) * mm, v(248.07, 45.8) * mm, v(246.32, 48.51) * mm, v(244.9, 50.5) * mm, v(243.4, 52.4) * mm, v(241.29, 54.83) * mm, v(238.44, 57.64) * mm, v(234.7, 60.63) * mm, v(230.64, 63.2) * mm, v(226.3, 65.27) * mm, v(221.7, 66.81) * mm, v(217.71, 67.61) * mm, v(214.45, 67.94) * mm, v(211.98, 68.02) * mm, v(209.52, 67.94) * mm, v(214.45, 67.94) * mm]});
            skFitSpline(sketch, "E15.0", {"points": [v(214.87, 74.28) * mm, v(211.98, 74.37) * mm, v(209.1, 74.28) * mm, v(205.28, 73.9) * mm, v(200.62, 72.96) * mm, v(195.27, 71.17) * mm, v(190.24, 68.76) * mm, v(185.58, 65.81) * mm, v(181.3, 62.4) * mm, v(178.06, 59.2) * mm, v(175.67, 56.45) * mm, v(173.98, 54.3) * mm, v(172.4, 52.08) * mm, v(170.44, 49.05) * mm, v(168.26, 45.12) * mm, v(166.07, 40.24) * mm, v(164.3, 35.2) * mm, v(162.91, 30.05) * mm, v(161.92, 24.8) * mm, v(161.42, 20.33) * mm, v(161.22, 16.73) * mm, v(161.17, 14.02) * mm, v(161.22, 11.3) * mm, v(161.42, 7.7) * mm, v(161.92, 3.24) * mm, v(162.91, -2.02) * mm, v(164.3, -7.18) * mm, v(166.07, -12.2) * mm, v(168.26, -17.1) * mm, v(170.44, -21.02) * mm, v(172.4, -24.05) * mm, v(173.98, -26.27) * mm, v(175.67, -28.42) * mm, v(178.06, -31.16) * mm, v(181.3, -34.36) * mm, v(185.58, -37.78) * mm, v(190.24, -40.73) * mm, v(195.27, -43.14) * mm, v(200.62, -44.93) * mm, v(205.28, -45.87) * mm, v(209.1, -46.25) * mm, v(211.98, -46.34) * mm, v(214.87, -46.25) * mm, v(218.69, -45.87) * mm, v(223.35, -44.93) * mm, v(228.7, -43.14) * mm, v(233.72, -40.73) * mm, v(238.4, -37.78) * mm, v(242.67, -34.36) * mm, v(245.9, -31.16) * mm, v(248.3, -28.42) * mm, v(249.99, -26.27) * mm, v(251.57, -24.05) * mm, v(253.53, -21.02) * mm, v(255.7, -17.1) * mm, v(257.9, -12.2) * mm, v(259.67, -7.18) * mm, v(261.06, -2.02) * mm, v(262.05, 3.24) * mm, v(262.55, 7.7) * mm, v(262.75, 11.3) * mm, v(262.8, 14.02) * mm, v(262.75, 16.73) * mm, v(262.55, 20.33) * mm, v(262.05, 24.8) * mm, v(261.06, 30.05) * mm, v(259.67, 35.2) * mm, v(257.9, 40.24) * mm, v(255.7, 45.12) * mm, v(253.53, 49.05) * mm, v(251.57, 52.08) * mm, v(249.99, 54.3) * mm, v(248.3, 56.45) * mm, v(245.9, 59.2) * mm, v(242.67, 62.4) * mm, v(238.4, 65.81) * mm, v(233.72, 68.76) * mm, v(228.7, 71.17) * mm, v(223.35, 72.96) * mm, v(218.69, 73.9) * mm, v(214.87, 74.28) * mm, v(211.98, 74.37) * mm, v(209.1, 74.28) * mm, v(214.87, 74.28) * mm]});
            skFitSpline(sketch, "E16.0", {"points": [v(215.3, 80.62) * mm, v(211.98, 80.73) * mm, v(208.68, 80.62) * mm, v(204.3, 80.18) * mm, v(198.97, 79.12) * mm, v(192.87, 77.06) * mm, v(187.16, 74.33) * mm, v(181.88, 71) * mm, v(177.07, 67.14) * mm, v(173.44, 63.56) * mm, v(170.78, 60.5) * mm, v(168.9, 58.11) * mm, v(167.14, 55.65) * mm, v(164.97, 52.3) * mm, v(162.57, 47.96) * mm, v(160.17, 42.6) * mm, v(158.22, 37.1) * mm, v(156.71, 31.47) * mm, v(155.63, 25.73) * mm, v(155.09, 20.88) * mm, v(154.87, 16.97) * mm, v(154.82, 14.02) * mm, v(154.87, 11.06) * mm, v(155.09, 7.15) * mm, v(155.63, 2.3) * mm, v(156.71, -3.44) * mm, v(158.22, -9.06) * mm, v(160.17, -14.57) * mm, v(162.57, -19.93) * mm, v(164.97, -24.26) * mm, v(167.14, -27.62) * mm, v(168.9, -30.08) * mm, v(170.78, -32.47) * mm, v(173.44, -35.53) * mm, v(177.07, -39.11) * mm, v(181.88, -42.96) * mm, v(187.16, -46.3) * mm, v(192.87, -49.03) * mm, v(198.97, -51.09) * mm, v(204.3, -52.15) * mm, v(208.68, -52.59) * mm, v(211.98, -52.7) * mm, v(215.3, -52.59) * mm, v(219.66, -52.15) * mm, v(225, -51.09) * mm, v(231.1, -49.03) * mm, v(236.8, -46.3) * mm, v(242.08, -42.96) * mm, v(246.9, -39.11) * mm, v(250.53, -35.53) * mm, v(253.19, -32.47) * mm, v(255.07, -30.08) * mm, v(256.83, -27.62) * mm, v(259, -24.26) * mm, v(261.4, -19.93) * mm, v(263.8, -14.57) * mm, v(265.75, -9.06) * mm, v(267.26, -3.44) * mm, v(268.34, 2.3) * mm, v(268.88, 7.15) * mm, v(269.1, 11.06) * mm, v(269.15, 14.02) * mm, v(269.1, 16.97) * mm, v(268.88, 20.88) * mm, v(268.34, 25.73) * mm, v(267.26, 31.47) * mm, v(265.75, 37.1) * mm, v(263.8, 42.6) * mm, v(261.4, 47.96) * mm, v(259, 52.3) * mm, v(256.83, 55.65) * mm, v(255.07, 58.11) * mm, v(253.19, 60.5) * mm, v(250.53, 63.56) * mm, v(246.9, 67.14) * mm, v(242.08, 71) * mm, v(236.8, 74.33) * mm, v(231.1, 77.06) * mm, v(225, 79.12) * mm, v(219.66, 80.18) * mm, v(215.3, 80.62) * mm, v(211.98, 80.73) * mm, v(208.68, 80.62) * mm, v(215.3, 80.62) * mm]});
            skFitSpline(sketch, "E17.0", {"points": [v(215.71, 86.96) * mm, v(211.98, 87.08) * mm, v(208.26, 86.96) * mm, v(203.33, 86.47) * mm, v(197.33, 85.27) * mm, v(190.48, 82.96) * mm, v(184.08, 79.9) * mm, v(178.19, 76.18) * mm, v(172.83, 71.9) * mm, v(168.83, 67.93) * mm, v(165.89, 64.55) * mm, v(163.81, 61.92) * mm, v(161.88, 59.22) * mm, v(159.5, 55.53) * mm, v(156.89, 50.8) * mm, v(154.27, 44.96) * mm, v(152.15, 38.98) * mm, v(150.52, 32.88) * mm, v(149.35, 26.68) * mm, v(148.76, 21.44) * mm, v(148.52, 17.2) * mm, v(148.46, 14.02) * mm, v(148.52, 10.82) * mm, v(148.76, 6.6) * mm, v(149.35, 1.35) * mm, v(150.52, -4.85) * mm, v(152.15, -10.95) * mm, v(154.27, -16.93) * mm, v(156.89, -22.77) * mm, v(159.5, -27.5) * mm, v(161.88, -31.19) * mm, v(163.81, -33.9) * mm, v(165.89, -36.52) * mm, v(168.83, -39.9) * mm, v(172.83, -43.86) * mm, v(178.19, -48.15) * mm, v(184.08, -51.87) * mm, v(190.48, -54.93) * mm, v(197.33, -57.24) * mm, v(203.33, -58.44) * mm, v(208.26, -58.93) * mm, v(211.98, -59.05) * mm, v(215.71, -58.93) * mm, v(220.63, -58.44) * mm, v(226.64, -57.24) * mm, v(233.49, -54.93) * mm, v(239.89, -51.87) * mm, v(245.78, -48.15) * mm, v(251.13, -43.86) * mm, v(255.14, -39.9) * mm, v(258.08, -36.52) * mm, v(260.15, -33.9) * mm, v(262.08, -31.19) * mm, v(264.46, -27.5) * mm, v(267.08, -22.77) * mm, v(269.7, -16.93) * mm, v(271.82, -10.95) * mm, v(273.45, -4.85) * mm, v(274.62, 1.35) * mm, v(275.2, 6.6) * mm, v(275.44, 10.82) * mm, v(275.5, 14.02) * mm, v(275.44, 17.2) * mm, v(275.2, 21.44) * mm, v(274.62, 26.68) * mm, v(273.45, 32.88) * mm, v(271.82, 38.98) * mm, v(269.7, 44.96) * mm, v(267.08, 50.8) * mm, v(264.46, 55.53) * mm, v(262.08, 59.22) * mm, v(260.15, 61.92) * mm, v(258.08, 64.55) * mm, v(255.14, 67.93) * mm, v(251.13, 71.9) * mm, v(245.78, 76.18) * mm, v(239.89, 79.9) * mm, v(233.49, 82.96) * mm, v(226.64, 85.27) * mm, v(220.63, 86.47) * mm, v(215.71, 86.96) * mm, v(211.98, 87.08) * mm, v(208.26, 86.96) * mm, v(215.71, 86.96) * mm]});
            skFitSpline(sketch, "E18.0", {"points": [v(216.13, 93.3) * mm, v(211.98, 93.44) * mm, v(207.84, 93.3) * mm, v(202.36, 92.75) * mm, v(195.69, 91.42) * mm, v(188.08, 88.86) * mm, v(181, 85.46) * mm, v(174.5, 81.36) * mm, v(168.6, 76.64) * mm, v(164.2, 72.3) * mm, v(161, 68.6) * mm, v(158.73, 65.73) * mm, v(156.63, 62.79) * mm, v(154.04, 58.78) * mm, v(151.2, 53.64) * mm, v(148.37, 47.32) * mm, v(146.08, 40.86) * mm, v(144.32, 34.29) * mm, v(143.06, 27.62) * mm, v(142.43, 21.99) * mm, v(142.18, 17.44) * mm, v(142.11, 14.02) * mm, v(142.18, 10.59) * mm, v(142.43, 6.04) * mm, v(143.06, 0.41) * mm, v(144.32, -6.26) * mm, v(146.08, -12.83) * mm, v(148.37, -19.29) * mm, v(151.2, -25.61) * mm, v(154.04, -30.75) * mm, v(156.63, -34.76) * mm, v(158.73, -37.7) * mm, v(161, -40.57) * mm, v(164.2, -44.27) * mm, v(168.6, -48.61) * mm, v(174.5, -53.33) * mm, v(181, -57.43) * mm, v(188.08, -60.83) * mm, v(195.69, -63.39) * mm, v(202.36, -64.72) * mm, v(207.84, -65.27) * mm, v(211.98, -65.4) * mm, v(216.13, -65.27) * mm, v(221.6, -64.72) * mm, v(228.28, -63.39) * mm, v(235.89, -60.83) * mm, v(242.97, -57.43) * mm, v(249.47, -53.33) * mm, v(255.37, -48.61) * mm, v(259.76, -44.27) * mm, v(262.98, -40.57) * mm, v(265.24, -37.7) * mm, v(267.34, -34.76) * mm, v(269.93, -30.75) * mm, v(272.77, -25.61) * mm, v(275.6, -19.29) * mm, v(277.89, -12.83) * mm, v(279.65, -6.26) * mm, v(280.9, 0.41) * mm, v(281.54, 6.04) * mm, v(281.8, 10.59) * mm, v(281.86, 14.02) * mm, v(281.8, 17.44) * mm, v(281.54, 21.99) * mm, v(280.9, 27.62) * mm, v(279.65, 34.29) * mm, v(277.89, 40.86) * mm, v(275.6, 47.32) * mm, v(272.77, 53.64) * mm, v(269.93, 58.78) * mm, v(267.34, 62.79) * mm, v(265.24, 65.73) * mm, v(262.98, 68.6) * mm, v(259.76, 72.3) * mm, v(255.37, 76.64) * mm, v(249.47, 81.36) * mm, v(242.97, 85.46) * mm, v(235.89, 88.86) * mm, v(228.28, 91.42) * mm, v(221.6, 92.75) * mm, v(216.13, 93.3) * mm, v(211.98, 93.44) * mm, v(207.84, 93.3) * mm, v(216.13, 93.3) * mm]});
            skFitSpline(sketch, "E19.0", {"points": [v(216.55, 99.64) * mm, v(211.98, 99.8) * mm, v(207.42, 99.64) * mm, v(201.39, 99.04) * mm, v(194.04, 97.57) * mm, v(185.69, 94.76) * mm, v(177.92, 91.03) * mm, v(170.8, 86.54) * mm, v(164.37, 81.4) * mm, v(159.59, 76.66) * mm, v(156.1, 72.66) * mm, v(153.65, 69.54) * mm, v(151.37, 66.35) * mm, v(148.58, 62.02) * mm, v(145.5, 56.48) * mm, v(142.46, 49.68) * mm, v(140, 42.74) * mm, v(138.12, 35.7) * mm, v(136.78, 28.56) * mm, v(136.1, 22.54) * mm, v(135.83, 17.68) * mm, v(135.76, 14.02) * mm, v(135.83, 10.35) * mm, v(136.1, 5.5) * mm, v(136.78, -0.53) * mm, v(138.12, -7.67) * mm, v(140, -14.71) * mm, v(142.46, -21.65) * mm, v(145.5, -28.45) * mm, v(148.58, -34) * mm, v(151.37, -38.32) * mm, v(153.65, -41.51) * mm, v(156.1, -44.62) * mm, v(159.59, -48.63) * mm, v(164.37, -53.36) * mm, v(170.8, -58.5) * mm, v(177.92, -63) * mm, v(185.69, -66.73) * mm, v(194.04, -69.54) * mm, v(201.39, -71) * mm, v(207.42, -71.6) * mm, v(211.98, -71.76) * mm, v(216.55, -71.6) * mm, v(222.58, -71) * mm, v(229.93, -69.54) * mm, v(238.28, -66.73) * mm, v(246.05, -63) * mm, v(253.17, -58.5) * mm, v(259.6, -53.36) * mm, v(264.38, -48.63) * mm, v(267.87, -44.62) * mm, v(270.32, -41.51) * mm, v(272.6, -38.32) * mm, v(275.4, -34) * mm, v(278.46, -28.45) * mm, v(281.5, -21.65) * mm, v(283.96, -14.71) * mm, v(285.85, -7.67) * mm, v(287.2, -0.53) * mm, v(287.87, 5.5) * mm, v(288.14, 10.35) * mm, v(288.2, 14.02) * mm, v(288.14, 17.68) * mm, v(287.87, 22.54) * mm, v(287.2, 28.56) * mm, v(285.85, 35.7) * mm, v(283.96, 42.74) * mm, v(281.5, 49.68) * mm, v(278.46, 56.48) * mm, v(275.4, 62.02) * mm, v(272.6, 66.35) * mm, v(270.32, 69.54) * mm, v(267.87, 72.66) * mm, v(264.38, 76.66) * mm, v(259.6, 81.4) * mm, v(253.17, 86.54) * mm, v(246.05, 91.03) * mm, v(238.28, 94.76) * mm, v(229.93, 97.57) * mm, v(222.58, 99.04) * mm, v(216.55, 99.64) * mm, v(211.98, 99.8) * mm, v(207.42, 99.64) * mm, v(216.55, 99.64) * mm]});
            skFitSpline(sketch, "E20.0", {"points": [v(216.97, 105.98) * mm, v(211.98, 106.15) * mm, v(207, 105.98) * mm, v(200.41, 105.33) * mm, v(192.4, 103.72) * mm, v(183.29, 100.65) * mm, v(174.83, 96.6) * mm, v(167.1, 91.72) * mm, v(160.14, 86.15) * mm, v(154.97, 81.03) * mm, v(151.2, 76.7) * mm, v(148.57, 73.35) * mm, v(146.12, 69.92) * mm, v(143.11, 65.26) * mm, v(139.82, 59.32) * mm, v(136.56, 52.04) * mm, v(133.94, 44.63) * mm, v(131.92, 37.11) * mm, v(130.49, 29.5) * mm, v(129.77, 23.09) * mm, v(129.48, 17.91) * mm, v(129.4, 14.02) * mm, v(129.48, 10.12) * mm, v(129.77, 4.94) * mm, v(130.49, -1.47) * mm, v(131.92, -9.08) * mm, v(133.94, -16.6) * mm, v(136.56, -24) * mm, v(139.82, -31.3) * mm, v(143.11, -37.23) * mm, v(146.12, -41.9) * mm, v(148.57, -45.32) * mm, v(151.2, -48.68) * mm, v(154.97, -53) * mm, v(160.14, -58.12) * mm, v(167.1, -63.69) * mm, v(174.83, -68.57) * mm, v(183.29, -72.62) * mm, v(192.4, -75.7) * mm, v(200.41, -77.3) * mm, v(207, -77.95) * mm, v(211.98, -78.12) * mm, v(216.97, -77.95) * mm, v(223.55, -77.3) * mm, v(231.57, -75.7) * mm, v(240.68, -72.62) * mm, v(249.13, -68.57) * mm, v(256.86, -63.69) * mm, v(263.83, -58.12) * mm, v(269, -53) * mm, v(272.76, -48.68) * mm, v(275.4, -45.32) * mm, v(277.85, -41.9) * mm, v(280.86, -37.23) * mm, v(284.15, -31.3) * mm, v(287.4, -24) * mm, v(290.03, -16.6) * mm, v(292.05, -9.08) * mm, v(293.48, -1.47) * mm, v(294.2, 4.94) * mm, v(294.49, 10.12) * mm, v(294.56, 14.02) * mm, v(294.49, 17.91) * mm, v(294.2, 23.09) * mm, v(293.48, 29.5) * mm, v(292.05, 37.11) * mm, v(290.03, 44.63) * mm, v(287.4, 52.04) * mm, v(284.15, 59.32) * mm, v(280.86, 65.26) * mm, v(277.85, 69.92) * mm, v(275.4, 73.35) * mm, v(272.76, 76.7) * mm, v(269, 81.03) * mm, v(263.83, 86.15) * mm, v(256.86, 91.72) * mm, v(249.13, 96.6) * mm, v(240.68, 100.65) * mm, v(231.57, 103.72) * mm, v(223.55, 105.33) * mm, v(216.97, 105.98) * mm, v(211.98, 106.15) * mm, v(207, 105.98) * mm, v(216.97, 105.98) * mm]});
            skFitSpline(sketch, "E21.0", {"points": [v(217.39, 112.32) * mm, v(211.98, 112.5) * mm, v(206.58, 112.32) * mm, v(199.44, 111.61) * mm, v(190.75, 109.87) * mm, v(180.9, 106.55) * mm, v(171.75, 102.17) * mm, v(163.41, 96.9) * mm, v(155.9, 90.9) * mm, v(150.35, 85.4) * mm, v(146.31, 80.76) * mm, v(143.48, 77.16) * mm, v(140.86, 73.49) * mm, v(137.65, 68.5) * mm, v(134.13, 62.16) * mm, v(130.66, 54.4) * mm, v(127.87, 46.5) * mm, v(125.73, 38.52) * mm, v(124.2, 30.44) * mm, v(123.44, 23.64) * mm, v(123.14, 18.15) * mm, v(123.06, 14.02) * mm, v(123.14, 9.88) * mm, v(123.44, 4.4) * mm, v(124.2, -2.41) * mm, v(125.73, -10.5) * mm, v(127.87, -18.48) * mm, v(130.66, -26.36) * mm, v(134.13, -34.13) * mm, v(137.65, -40.48) * mm, v(140.86, -45.46) * mm, v(143.48, -49.13) * mm, v(146.31, -52.73) * mm, v(150.35, -57.37) * mm, v(155.9, -62.87) * mm, v(163.41, -68.87) * mm, v(171.75, -74.14) * mm, v(180.9, -78.52) * mm, v(190.75, -81.84) * mm, v(199.44, -83.58) * mm, v(206.58, -84.3) * mm, v(211.98, -84.47) * mm, v(217.39, -84.3) * mm, v(224.53, -83.58) * mm, v(233.21, -81.84) * mm, v(243.07, -78.52) * mm, v(252.22, -74.14) * mm, v(260.56, -68.87) * mm, v(268.06, -62.87) * mm, v(273.62, -57.37) * mm, v(277.65, -52.73) * mm, v(280.48, -49.13) * mm, v(283.1, -45.46) * mm, v(286.32, -40.48) * mm, v(289.84, -34.13) * mm, v(293.31, -26.36) * mm, v(296.1, -18.48) * mm, v(298.24, -10.5) * mm, v(299.76, -2.41) * mm, v(300.53, 4.4) * mm, v(300.83, 9.88) * mm, v(300.9, 14.02) * mm, v(300.83, 18.15) * mm, v(300.53, 23.64) * mm, v(299.76, 30.44) * mm, v(298.24, 38.52) * mm, v(296.1, 46.5) * mm, v(293.31, 54.4) * mm, v(289.84, 62.16) * mm, v(286.32, 68.5) * mm, v(283.1, 73.49) * mm, v(280.48, 77.16) * mm, v(277.65, 80.76) * mm, v(273.62, 85.4) * mm, v(268.06, 90.9) * mm, v(260.56, 96.9) * mm, v(252.22, 102.17) * mm, v(243.07, 106.55) * mm, v(233.21, 109.87) * mm, v(224.53, 111.61) * mm, v(217.39, 112.32) * mm, v(211.98, 112.5) * mm, v(206.58, 112.32) * mm, v(217.39, 112.32) * mm]});
            skFitSpline(sketch, "E22.0", {"points": [v(217.8, 118.66) * mm, v(211.98, 118.85) * mm, v(206.16, 118.66) * mm, v(198.47, 117.9) * mm, v(189.1, 116.02) * mm, v(178.5, 112.45) * mm, v(168.67, 107.74) * mm, v(159.72, 102.08) * mm, v(151.68, 95.65) * mm, v(145.73, 89.77) * mm, v(141.42, 84.8) * mm, v(138.4, 80.98) * mm, v(135.6, 77.06) * mm, v(132.18, 71.75) * mm, v(128.44, 65) * mm, v(124.75, 56.75) * mm, v(121.8, 48.4) * mm, v(119.53, 39.93) * mm, v(117.92, 31.38) * mm, v(117.11, 24.19) * mm, v(116.79, 18.39) * mm, v(116.7, 14.02) * mm, v(116.79, 9.64) * mm, v(117.11, 3.84) * mm, v(117.92, -3.35) * mm, v(119.53, -11.9) * mm, v(121.8, -20.36) * mm, v(124.75, -28.72) * mm, v(128.44, -36.97) * mm, v(132.18, -43.72) * mm, v(135.6, -49.03) * mm, v(138.4, -52.95) * mm, v(141.42, -56.78) * mm, v(145.73, -61.74) * mm, v(151.68, -67.62) * mm, v(159.72, -74.05) * mm, v(168.67, -79.7) * mm, v(178.5, -84.42) * mm, v(189.1, -88) * mm, v(198.47, -89.87) * mm, v(206.16, -90.63) * mm, v(211.98, -90.82) * mm, v(217.8, -90.63) * mm, v(225.5, -89.87) * mm, v(234.86, -88) * mm, v(245.47, -84.42) * mm, v(255.3, -79.7) * mm, v(264.25, -74.05) * mm, v(272.3, -67.62) * mm, v(278.23, -61.74) * mm, v(282.55, -56.78) * mm, v(285.57, -52.95) * mm, v(288.36, -49.03) * mm, v(291.79, -43.72) * mm, v(295.52, -36.97) * mm, v(299.21, -28.72) * mm, v(302.17, -20.36) * mm, v(304.44, -11.9) * mm, v(306.05, -3.35) * mm, v(306.86, 3.84) * mm, v(307.18, 9.64) * mm, v(307.26, 14.02) * mm, v(307.18, 18.39) * mm, v(306.86, 24.19) * mm, v(306.05, 31.38) * mm, v(304.44, 39.93) * mm, v(302.17, 48.4) * mm, v(299.21, 56.75) * mm, v(295.52, 65) * mm, v(291.79, 71.75) * mm, v(288.36, 77.06) * mm, v(285.57, 80.98) * mm, v(282.55, 84.8) * mm, v(278.23, 89.77) * mm, v(272.3, 95.65) * mm, v(264.25, 102.08) * mm, v(255.3, 107.74) * mm, v(245.47, 112.45) * mm, v(234.86, 116.02) * mm, v(225.5, 117.9) * mm, v(217.8, 118.66) * mm, v(211.98, 118.85) * mm, v(206.16, 118.66) * mm, v(217.8, 118.66) * mm]});
            skPoint(sketch, "E23", {"position": v(0, 101.6) * mm});
            skPoint(sketch, "E24", {"position": v(0, -101.6) * mm});
            skPoint(sketch, "E24.positionSnap0", {"position": v(0, -38.1) * mm});
            skPoint(sketch, "E25", {"position": v(211.98, 118.8) * mm});
            skPoint(sketch, "E26", {"position": v(211.98, -90.76) * mm});
            skPoint(sketch, "E26.positionSnap0", {"position": v(211.98, -24.08) * mm});
            skSolve(sketch);
        }
        {
            var Q0;
            Q0=makeQuery(id+"F0.imprint","IMPRINT",FACE,{"disambiguationData":[TD([[makeQuery(id+"F0.imprint","IMPRINT",EDGE,{"derivedFrom":sQuery(id+"F0.wireOp",EDGE,"E8.0")}),-1.0]])]});
            var Q1;
            Q1=makeQuery(id+"F0.imprint","IMPRINT",FACE,{"disambiguationData":[TD([[makeQuery(id+"F0.imprint","IMPRINT",EDGE,{"derivedFrom":sQuery(id+"F0.wireOp",EDGE,"E7.0")}),-1.0]])]});
            var Q2;
            Q2=makeQuery(id+"F0.imprint","IMPRINT",FACE,{"disambiguationData":[TD([[makeQuery(id+"F0.imprint","IMPRINT",EDGE,{"derivedFrom":sQuery(id+"F0.wireOp",EDGE,"E6.0")}),-1.0]])]});
            var Q3;
            Q3=makeQuery(id+"F0.imprint","IMPRINT",FACE,{"disambiguationData":[TD([[makeQuery(id+"F0.imprint","IMPRINT",EDGE,{"derivedFrom":sQuery(id+"F0.wireOp",EDGE,"E9.0")}),-1.0]])]});
            var Q4;
            Q4=makeQuery(id+"F0.imprint","IMPRINT",FACE,{"disambiguationData":[TD([[makeQuery(id+"F0.imprint","IMPRINT",EDGE,{"derivedFrom":sQuery(id+"F0.wireOp",EDGE,"E5.0")}),-1.0]])]});
            var Q5;
            Q5=makeQuery(id+"F0.imprint","IMPRINT",FACE,{"disambiguationData":[TD([[makeQuery(id+"F0.imprint","IMPRINT",EDGE,{"derivedFrom":sQuery(id+"F0.wireOp",EDGE,"E4.0")}),-1.0]])]});
            var Q6;
            Q6=makeQuery(id+"F0.imprint","IMPRINT",FACE,{"disambiguationData":[TD([[makeQuery(id+"F0.imprint","IMPRINT",EDGE,{"derivedFrom":sQuery(id+"F0.wireOp",EDGE,"E3.0")}),-1.0]])]});
            var Q7;
            Q7=makeQuery(id+"F0.imprint","IMPRINT",FACE,{"disambiguationData":[TD([[makeQuery(id+"F0.imprint","IMPRINT",EDGE,{"derivedFrom":sQuery(id+"F0.wireOp",EDGE,"E2.0")}),-1.0]])]});
            var Q8;
            Q8=makeQuery(id+"F0.imprint","IMPRINT",FACE,{"disambiguationData":[TD([[makeQuery(id+"F0.imprint","IMPRINT",EDGE,{"derivedFrom":sQuery(id+"F0.wireOp",EDGE,"E1.0")}),-1.0]])]});
            var Q9;
            Q9=makeQuery(id+"F0.imprint","IMPRINT",FACE,{"disambiguationData":[TD([[makeQuery(id+"F0.imprint","IMPRINT",EDGE,{"derivedFrom":sQuery(id+"F0.wireOp",EDGE,"E0")}),-1.0]])]});
            var Q10;
            Q10=makeQuery(id+"F0.imprint","IMPRINT",FACE,{"disambiguationData":[TD([[makeQuery(id+"F0.imprint","IMPRINT",EDGE,{"derivedFrom":sQuery(id+"F0.wireOp",EDGE,"E0")}),1.0]])]});
            var Q11;
            Q11=makeQuery(id+"F0.imprint","IMPRINT",FACE,{"disambiguationData":[TD([[makeQuery(id+"F0.imprint","IMPRINT",EDGE,{"derivedFrom":sQuery(id+"F0.wireOp",EDGE,"E11")}),1.0]])]});
            var Q12;
            Q12=makeQuery(id+"F0.imprint","IMPRINT",FACE,{"disambiguationData":[TD([[makeQuery(id+"F0.imprint","IMPRINT",EDGE,{"derivedFrom":sQuery(id+"F0.wireOp",EDGE,"E19.0")}),-1.0]])]});
            var Q13;
            Q13=makeQuery(id+"F0.imprint","IMPRINT",FACE,{"disambiguationData":[TD([[makeQuery(id+"F0.imprint","IMPRINT",EDGE,{"derivedFrom":sQuery(id+"F0.wireOp",EDGE,"E15.0")}),-1.0]])]});
            var Q14;
            Q14=makeQuery(id+"F0.imprint","IMPRINT",FACE,{"disambiguationData":[TD([[makeQuery(id+"F0.imprint","IMPRINT",EDGE,{"derivedFrom":sQuery(id+"F0.wireOp",EDGE,"E11")}),-1.0]])]});
            var Q15;
            Q15=makeQuery(id+"F0.imprint","IMPRINT",FACE,{"disambiguationData":[TD([[makeQuery(id+"F0.imprint","IMPRINT",EDGE,{"derivedFrom":sQuery(id+"F0.wireOp",EDGE,"E16.0")}),-1.0]])]});
            var Q16;
            Q16=makeQuery(id+"F0.imprint","IMPRINT",FACE,{"disambiguationData":[TD([[makeQuery(id+"F0.imprint","IMPRINT",EDGE,{"derivedFrom":sQuery(id+"F0.wireOp",EDGE,"E21.0")}),-1.0]])]});
            var Q17;
            Q17=makeQuery(id+"F0.imprint","IMPRINT",FACE,{"disambiguationData":[TD([[makeQuery(id+"F0.imprint","IMPRINT",EDGE,{"derivedFrom":sQuery(id+"F0.wireOp",EDGE,"E13.0")}),-1.0]])]});
            var Q18;
            Q18=makeQuery(id+"F0.imprint","IMPRINT",FACE,{"disambiguationData":[TD([[makeQuery(id+"F0.imprint","IMPRINT",EDGE,{"derivedFrom":sQuery(id+"F0.wireOp",EDGE,"E14.0")}),-1.0]])]});
            var Q19;
            Q19=makeQuery(id+"F0.imprint","IMPRINT",FACE,{"disambiguationData":[TD([[makeQuery(id+"F0.imprint","IMPRINT",EDGE,{"derivedFrom":sQuery(id+"F0.wireOp",EDGE,"E12.0")}),-1.0]])]});
            var Q20;
            Q20=makeQuery(id+"F0.imprint","IMPRINT",FACE,{"disambiguationData":[TD([[makeQuery(id+"F0.imprint","IMPRINT",EDGE,{"derivedFrom":sQuery(id+"F0.wireOp",EDGE,"E17.0")}),-1.0]])]});
            var Q21;
            Q21=makeQuery(id+"F0.imprint","IMPRINT",FACE,{"disambiguationData":[TD([[makeQuery(id+"F0.imprint","IMPRINT",EDGE,{"derivedFrom":sQuery(id+"F0.wireOp",EDGE,"E18.0")}),-1.0]])]});
            var Q22;
            Q22=makeQuery(id+"F0.imprint","IMPRINT",FACE,{"disambiguationData":[TD([[makeQuery(id+"F0.imprint","IMPRINT",EDGE,{"derivedFrom":sQuery(id+"F0.wireOp",EDGE,"E20.0")}),-1.0]])]});
            extrude(context, id + "F1", {"entities" : qUnion([Q0, Q1, Q2, Q3, Q4, Q5, Q6, Q7, Q8, Q9, Q10, Q11, Q12, Q13, Q14, Q15, Q16, Q17, Q18, Q19, Q20, Q21, Q22]), "depth" : 3.17 * mm});
        }
    });
